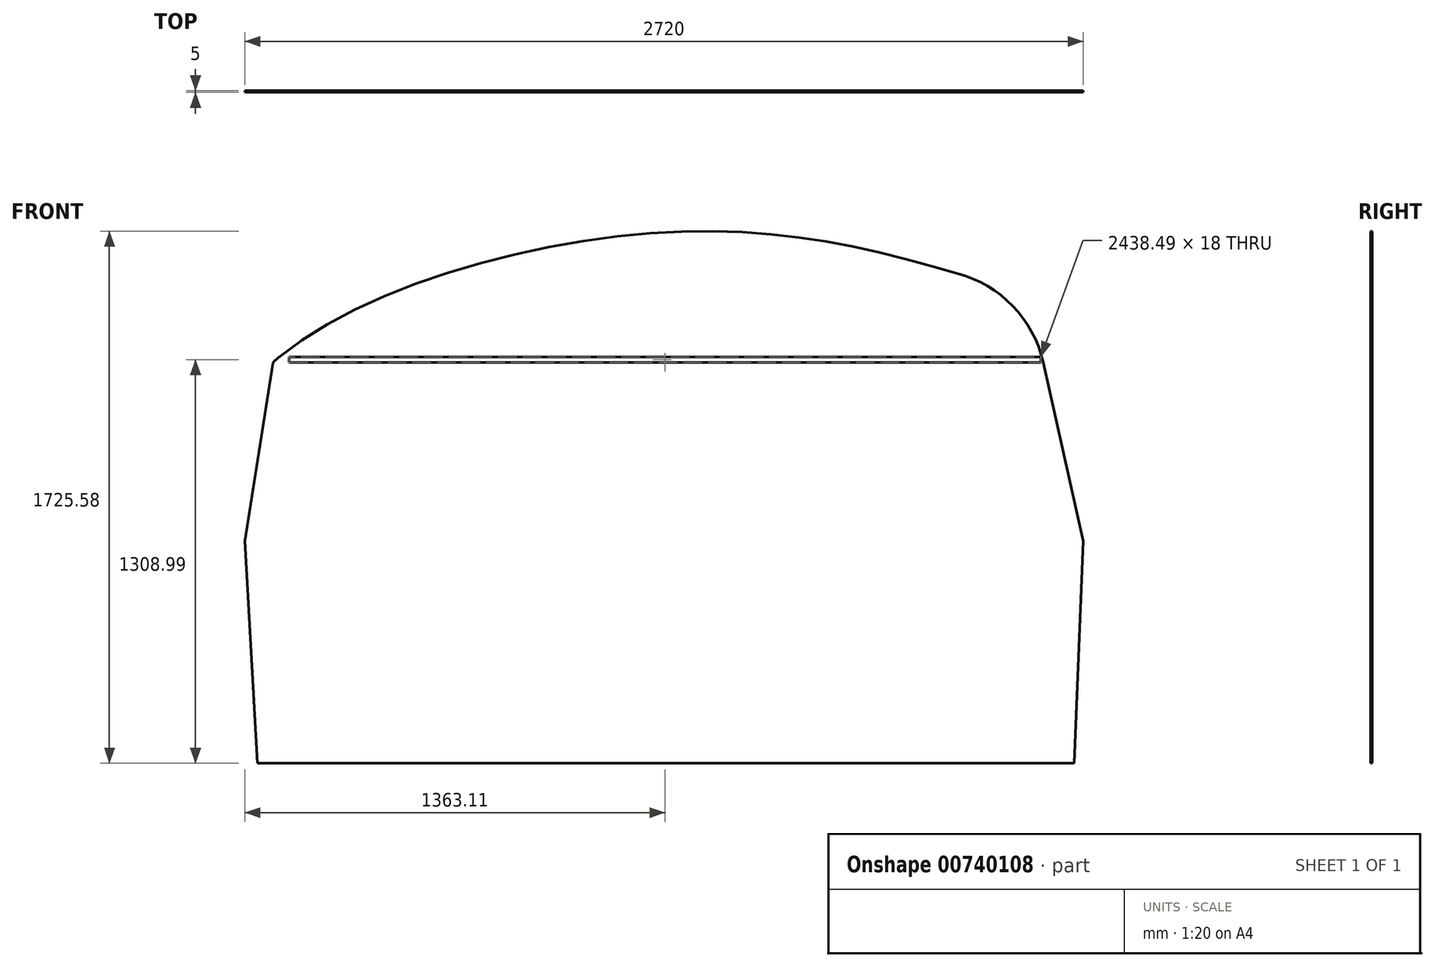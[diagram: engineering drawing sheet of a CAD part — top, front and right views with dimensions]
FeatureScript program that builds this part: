
annotation { "Feature Type Name" : "Feature", "Feature Type Description" : "" }
export const myFeature = defineFeature(function(context is Context, id is Id, definition is map)
    precondition{}
    {
        {
            var Q0;
            Q0=qCreatedBy(makeId("Front.planeOp"),FACE);
            var sketch = newSketch(context, id + "F0", { "sketchPlane" : qUnion([Q0])});
            skLineSegment(sketch, "E0", {"start": v(-1301.84, -2680.64) * mm, "end": v(-1272.28, -1960.64) * mm});
            skLineSegment(sketch, "E1", {"start": v(-3992.28, -1960.64) * mm, "end": v(-3951.84, -2680.64) * mm});
            skLineSegment(sketch, "E2", {"start": v(-2351.84, -2680.64) * mm, "end": v(-1751.84, -2680.64) * mm});
            skLineSegment(sketch, "E3", {"start": v(-1751.84, -2680.64) * mm, "end": v(-1751.84, -2680.64) * mm});
            skLineSegment(sketch, "E4", {"start": v(-1751.84, -2680.64) * mm, "end": v(-1301.84, -2680.64) * mm});
            skLineSegment(sketch, "E5", {"start": v(-3951.84, -2680.64) * mm, "end": v(-2351.84, -2680.64) * mm});
            skLineSegment(sketch, "E6", {"start": v(-3992.28, -1960.64) * mm, "end": v(-1272.28, -1960.64) * mm});
            skLineSegment(sketch, "E7", {"start": v(-1272.28, -1960.64) * mm, "end": v(-1402.73, -1380.64) * mm});
            skArc(sketch, "E8", {"start": v(-1402.73, -1380.64) * mm, "mid": v(-1501.3, -1197.8) * mm, "end": v(-1680.52, -1092.8) * mm});
            skLineSegment(sketch, "E9", {"start": v(-3992.28, -1960.64) * mm, "end": v(-3900.82, -1380.64) * mm});
            skFitSpline(sketch, "E10", {"points": [v(-3900.82, -1380.64) * mm, v(-2660.78, -960.64) * mm, v(-1680.52, -1092.8) * mm], "startDerivative": vector(1516.26, 1331.67) * mm, "endDerivative": vector(1973.4, -585.85) * mm});
            skLineSegment(sketch, "E11", {"start": v(-3900.82, -1380.64) * mm, "end": v(-1402.73, -1380.64) * mm});
            skLineSegment(sketch, "E12.bottom", {"start": v(-3848.42, -1380.64) * mm, "end": v(-1409.92, -1380.64) * mm});
            skLineSegment(sketch, "E12.left", {"start": v(-3848.42, -1380.64) * mm, "end": v(-3848.42, -1362.64) * mm});
            skLineSegment(sketch, "E12.right", {"start": v(-1409.92, -1380.64) * mm, "end": v(-1409.92, -1362.64) * mm});
            skLineSegment(sketch, "E13", {"start": v(-1409.92, -1380.64) * mm, "end": v(-1402.73, -1380.64) * mm});
            skLineSegment(sketch, "E14", {"start": v(-1409.92, -1362.64) * mm, "end": v(-1407.24, -1362.64) * mm});
            skLineSegment(sketch, "E15", {"start": v(-3848.42, -1362.64) * mm, "end": v(-3879.62, -1362.64) * mm});
            skLineSegment(sketch, "E16", {"start": v(-1409.92, -1362.64) * mm, "end": v(-3848.42, -1362.64) * mm});
            skSolve(sketch);
        }
        {
            var Q0;
            Q0 = qSketchRegion(id + "F0", true);
            extrude(context, id + "F1", {"entities" : qUnion([Q0]), "depth" : 5 * mm, "offsetDistance" : 25 * mm});
        }
    });
